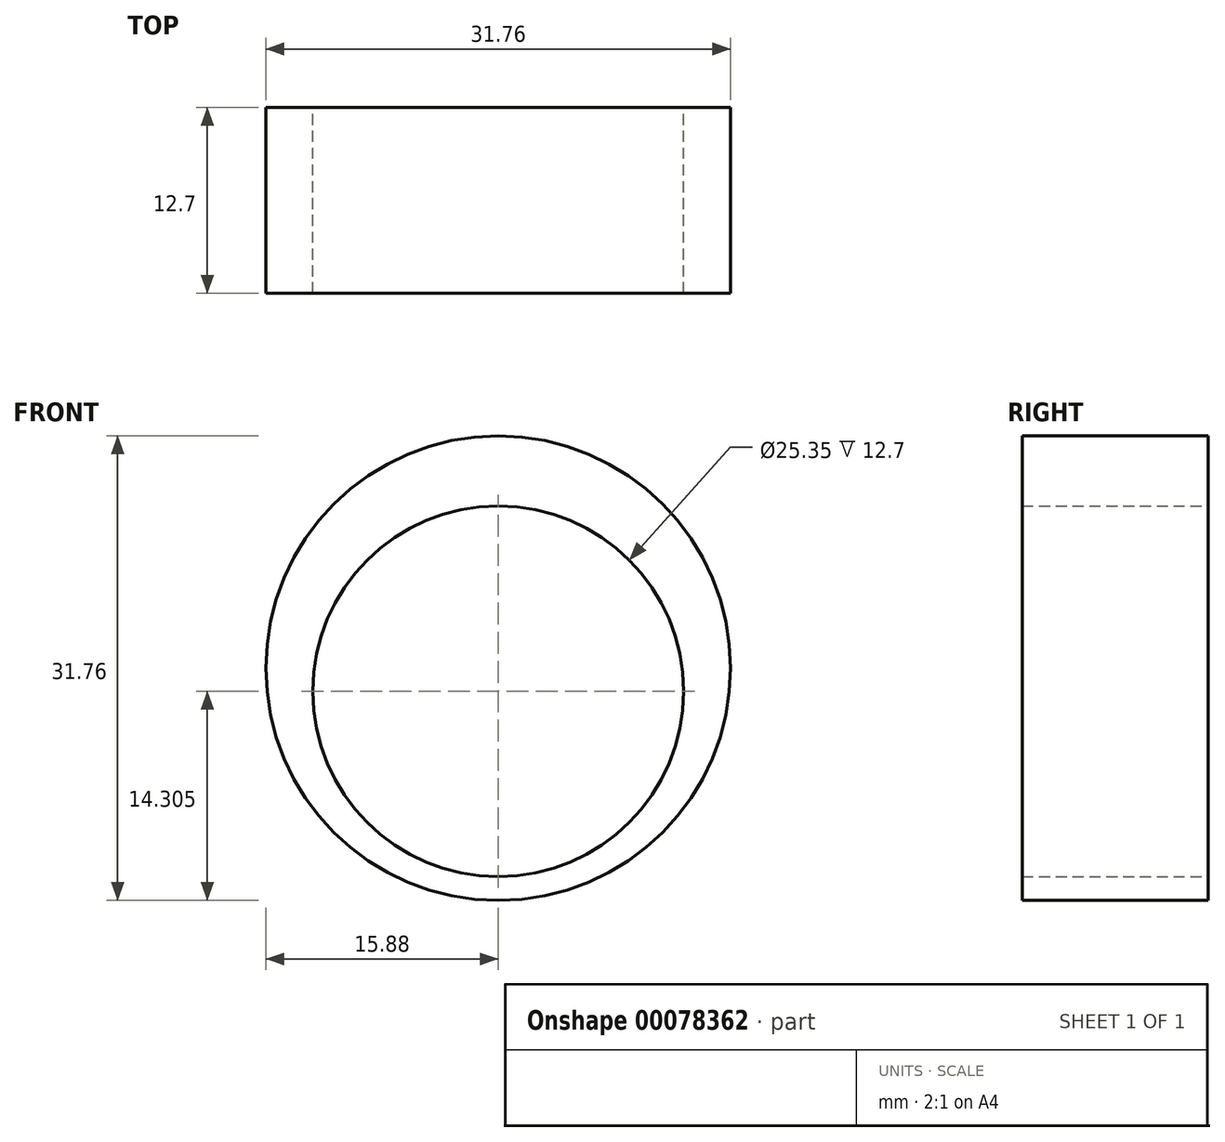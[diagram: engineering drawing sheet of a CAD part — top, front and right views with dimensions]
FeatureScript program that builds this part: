
annotation { "Feature Type Name" : "Feature", "Feature Type Description" : "" }
export const myFeature = defineFeature(function(context is Context, id is Id, definition is map)
    precondition{}
    {
        {
            var Q0;
            Q0=qCreatedBy(makeId("Front.planeOp"),FACE);
            var sketch = newSketch(context, id + "F0", { "sketchPlane" : qUnion([Q0])});
            skCircle(sketch, "E0", {"center": v(0, 0) * mm, "radius": 15.88 * mm});
            skCircle(sketch, "E1", {"center": v(0, -1.57) * mm, "radius": 12.67 * mm});
            skSolve(sketch);
        }
        {
            var Q0;
            Q0 = qSketchRegion(id + "F0", true);
            extrude(context, id + "F1", {"entities" : qUnion([Q0]), "depth" : 12.7 * mm});
        }
    });
